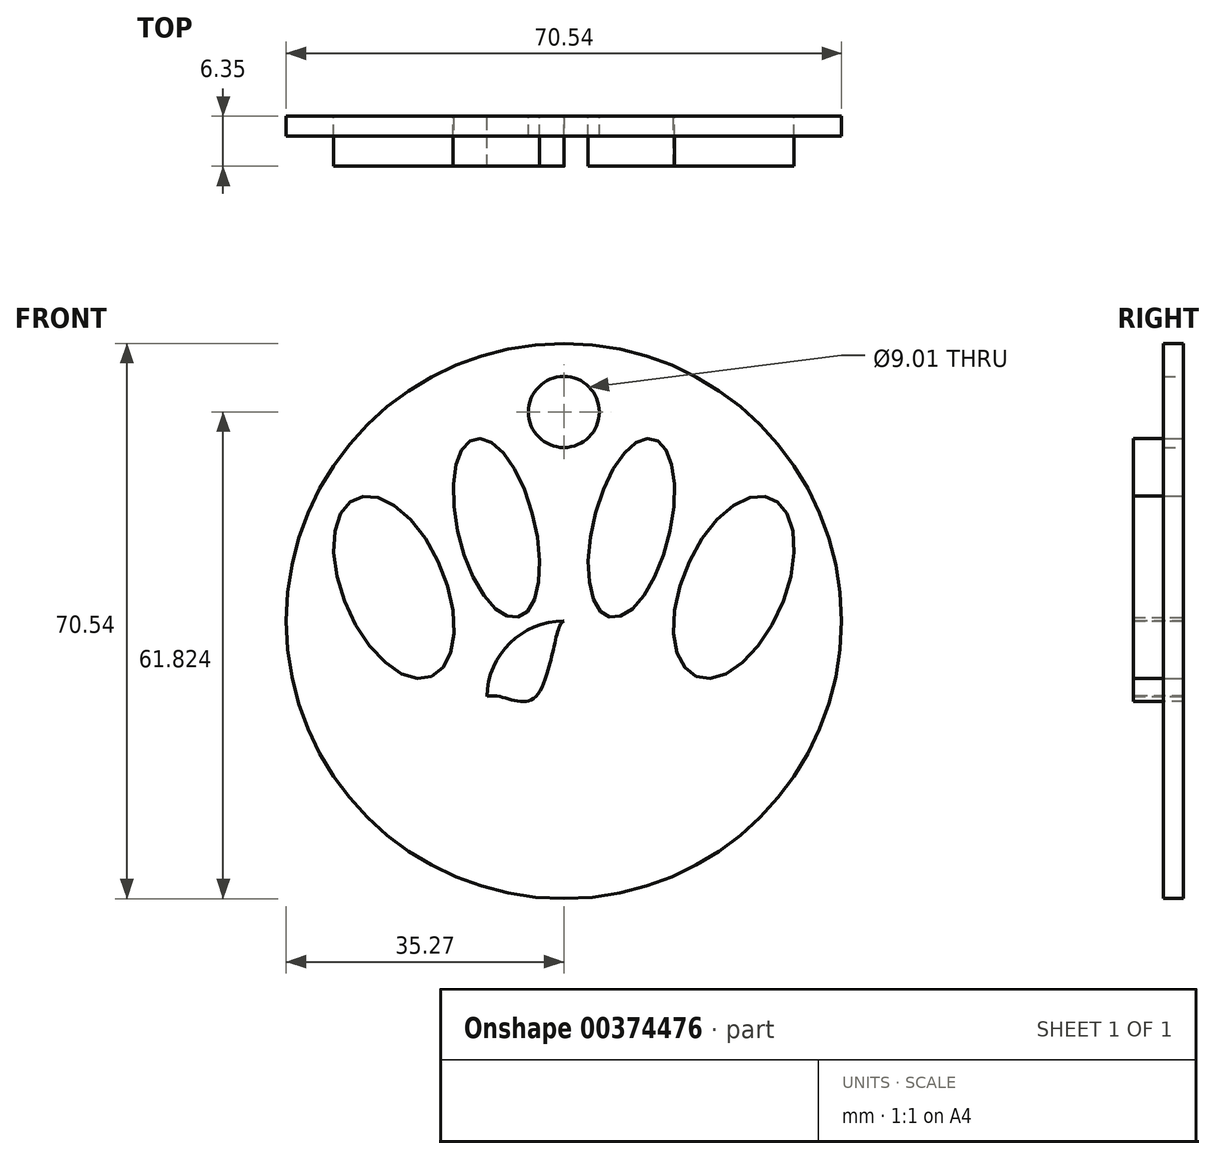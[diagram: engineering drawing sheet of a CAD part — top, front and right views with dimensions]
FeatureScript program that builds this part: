
annotation { "Feature Type Name" : "Feature", "Feature Type Description" : "" }
export const myFeature = defineFeature(function(context is Context, id is Id, definition is map)
    precondition{}
    {
        {
            var Q0;
            Q0=qCreatedBy(makeId("Front.planeOp"),FACE);
            var sketch = newSketch(context, id + "F0", { "sketchPlane" : qUnion([Q0])});
            skCircle(sketch, "E0", {"center": v(0, 0) * mm, "radius": 36.83 * mm});
            skArc(sketch, "E1", {"start": v(0, 0) * mm, "mid": v(-6.85, -2.8) * mm, "end": v(-9.77, -9.61) * mm});
            skFitSpline(sketch, "E2", {"points": [v(-9.77, -9.61) * mm, v(-13.7, -14.9) * mm, v(-20.9, -14.56) * mm, v(-21.59, -23.13) * mm, v(0, -27.59) * mm, v(0, 0) * mm, v(-3.77, -9.77) * mm, v(-9.77, -9.61) * mm]});
            skLineSegment(sketch, "E3", {"start": v(0, 36.83) * mm, "end": v(0, -36.83) * mm});
            skArc(sketch, "E4.MirrorCS", {"start": v(0, 0) * mm, "mid": v(6.85, -2.8) * mm, "end": v(9.77, -9.61) * mm});
            skFitSpline(sketch, "E5.MirrorCS", {"points": [v(9.77, -9.61) * mm, v(13.7, -14.9) * mm, v(20.9, -14.56) * mm, v(21.59, -23.13) * mm, v(0, -27.59) * mm, v(0, 0) * mm, v(3.77, -9.77) * mm, v(9.77, -9.61) * mm]});
            skFitSpline(sketch, "E6", {"points": [v(-5.13, -30.37) * mm, v(4.65, -30.28) * mm, v(3.43, -55.34) * mm, v(-5.13, -30.37) * mm]});
            skEllipse(sketch, "E7", {"center": v(-21.59, 4.28) * mm, "majorRadius": 12.28 * mm, "minorRadius": 6.48 * mm, "majorAxis": v(0.4, -0.92)});
            skEllipse(sketch, "E8", {"center": v(-8.57, 11.82) * mm, "majorRadius": 11.64 * mm, "minorRadius": 4.89 * mm, "majorAxis": v(0.24, -0.97)});
            skEllipse(sketch, "E9.MirrorC", {"center": v(8.57, 11.82) * mm, "majorRadius": 11.64 * mm, "minorRadius": 4.89 * mm, "majorAxis": v(-0.24, -0.97)});
            skEllipse(sketch, "E10.MirrorC", {"center": v(21.59, 4.28) * mm, "majorRadius": 12.28 * mm, "minorRadius": 6.48 * mm, "majorAxis": v(-0.4, -0.92)});
            skSolve(sketch);
        }
        {
            var Q0;
            Q0=makeQuery(id+"F0.imprint","IMPRINT",FACE,{"disambiguationData":[TD([[makeQuery(id+"F0.imprint","IMPRINT",EDGE,{"derivedFrom":sQuery(id+"F0.wireOp",EDGE,"E8")}),1.0]])]});
            var Q1;
            Q1=makeQuery(id+"F0.imprint","IMPRINT",FACE,{"disambiguationData":[TD([[makeQuery(id+"F0.imprint","IMPRINT",EDGE,{"derivedFrom":sQuery(id+"F0.wireOp",EDGE,"E7")}),1.0]])]});
            var Q2;
            Q2=makeQuery(id+"F0.imprint","IMPRINT",FACE,{"disambiguationData":[TD([[makeQuery(id+"F0.imprint","IMPRINT",EDGE,{"derivedFrom":sQuery(id+"F0.wireOp",EDGE,"E9.MirrorC")}),1.0]])]});
            var Q3;
            Q3=makeQuery(id+"F0.imprint","IMPRINT",FACE,{"disambiguationData":[TD([[makeQuery(id+"F0.imprint","IMPRINT",EDGE,{"derivedFrom":sQuery(id+"F0.wireOp",EDGE,"E10.MirrorC")}),1.0]])]});
            var Q4;
            {var subQ0=sQuery(id+"F0.wireOp",EDGE,"E4.MirrorCS");Q4=makeQuery(id+"F0.imprint","IMPRINT",FACE,{"disambiguationData":[TD([[makeQuery(id+"F0.imprint","IMPRINT",EDGE,{"derivedFrom":subQ0}),-1.0]])]});}
            var Q5;
            {var subQ0=sQuery(id+"F0.wireOp",EDGE,"E1");Q5=makeQuery(id+"F0.imprint","IMPRINT",FACE,{"disambiguationData":[TD([[makeQuery(id+"F0.imprint","IMPRINT",EDGE,{"derivedFrom":subQ0}),1.0]])]});}
            extrude(context, id + "F1", {"entities" : qUnion([Q0, Q1, Q2, Q3, Q4, Q5]), "depth" : 6.35 * mm});
        }
        {
            var Q0;
            Q0=qCreatedBy(makeId("Front.planeOp"),FACE);
            var sketch = newSketch(context, id + "F2", { "sketchPlane" : qUnion([Q0])});
            skCircle(sketch, "E11", {"center": v(0, 0) * mm, "radius": 40.98 * mm});
            skCircle(sketch, "E12", {"center": v(0, 0) * mm, "radius": 35.6 * mm});
            skSolve(sketch);
        }
        {
            var Q0;
            Q0 = qSketchRegion(id + "F2", true);
            extrude(context, id + "F3", {"entities" : qUnion([Q0]), "depth" : 6.35 * mm});
        }
        {
            var Q0;
            Q0=makeQuery(id+"F3.opExtrude","SWEPT_BODY",BODY,{"disambiguationData":[OSD([sQuery(id+"F2.wireOp",EDGE,"E11"),sQuery(id+"F2.wireOp",EDGE,"E12")])]});
            deleteBodies(context, id + "F4", {"entities" : qUnion([Q0])});
        }
        {
            var Q0;
            Q0=qCreatedBy(makeId("Front.planeOp"),FACE);
            var sketch = newSketch(context, id + "F5", { "sketchPlane" : qUnion([Q0])});
            skCircle(sketch, "E13", {"center": v(0, 0) * mm, "radius": 35.27 * mm});
            skSolve(sketch);
        }
        {
            var Q0;
            Q0=makeQuery(id+"F5.imprint","IMPRINT",FACE,{"disambiguationData":[TD([[makeQuery(id+"F5.imprint","IMPRINT",EDGE,{"derivedFrom":sQuery(id+"F5.wireOp",EDGE,"E13")}),1.0]])]});
            extrude(context, id + "F6", {"entities" : qUnion([Q0]), "depth" : 2.54 * mm});
        }
        {
            var Q0;
            Q0=qCreatedBy(makeId("Front.planeOp"),FACE);
            var sketch = newSketch(context, id + "F7", { "sketchPlane" : qUnion([Q0])});
            skCircle(sketch, "E14", {"center": v(0, 26.55) * mm, "radius": 4.5 * mm});
            skSolve(sketch);
        }
        {
            var Q0;
            Q0 = qSketchRegion(id + "F7", true);
            extrude(context, id + "F8", {"entities" : qUnion([Q0]), "operationType" : NewBodyOperationType.REMOVE, "depth" : 2.54 * mm});
        }
    });
